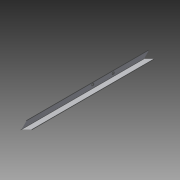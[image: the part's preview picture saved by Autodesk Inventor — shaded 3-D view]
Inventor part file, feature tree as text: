
AUTODESK INVENTOR PART (.ipt)
format: ipt  version: 2014 SP1 (Build 180222100, 222)  size: 106,496 bytes
history: native  units: in
note: dims shown in document units (in); Inventor stores cm internally (conversion verified against a paired STEP export)
features: reference x5, extrude x2, sketch x2
ambient origin geometry x8: Origin, YZ Plane, XZ Plane, XY Plane, X Axis, Y Axis, Z Axis, Center Point
bodies: Solid1 (feature_tree)
feature tree (9):
  extrude  "Extrusion1"  Depth=0.0312in
  extrude  "Extrusion2"  Depth=18.9688in TaperAngle=0.0deg
  sketch  "Sketch1"  dims[d0=0.625in d1=0.0312in]
  sketch  "Sketch2"  dims[d2=18.9688in d3=0.0in d4=1.0in d5=0.0in d6=0.266in]
  reference  "Reference1"
  reference  "Reference2"
  reference  "Reference3"
  reference  "Reference4"
  reference  "Reference5"
